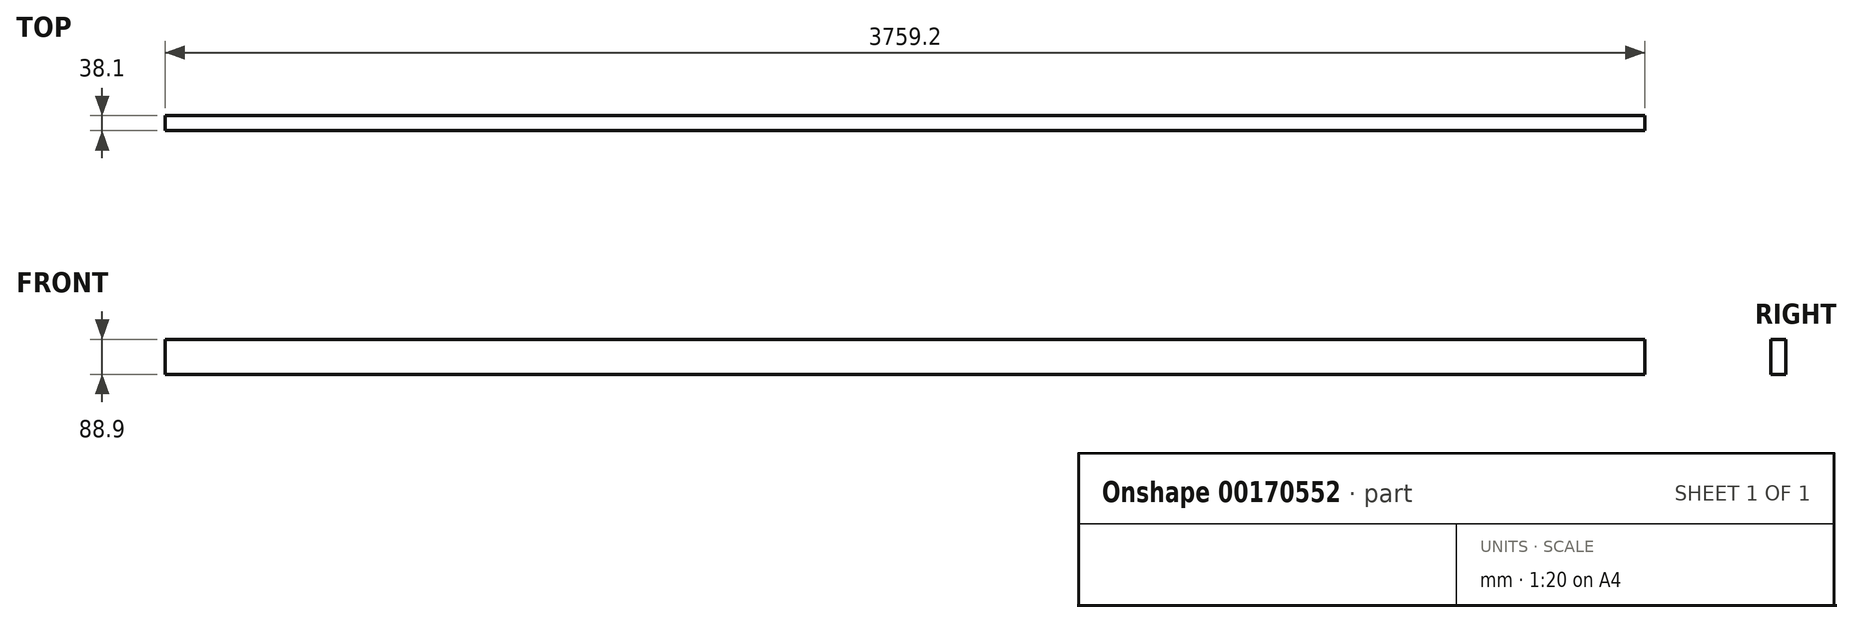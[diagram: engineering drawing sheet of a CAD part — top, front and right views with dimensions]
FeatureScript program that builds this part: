
annotation { "Feature Type Name" : "Feature", "Feature Type Description" : "" }
export const myFeature = defineFeature(function(context is Context, id is Id, definition is map)
    precondition{}
    {
        {
            var Q0;
            Q0=qCreatedBy(makeId("Right.planeOp"),FACE);
            var sketch = newSketch(context, id + "F0", { "sketchPlane" : qUnion([Q0])});
            skLineSegment(sketch, "E0.bottom", {"start": v(0, 0) * mm, "end": v(38.1, 0) * mm});
            skLineSegment(sketch, "E0.top", {"start": v(0, 88.9) * mm, "end": v(38.1, 88.9) * mm});
            skLineSegment(sketch, "E0.left", {"start": v(0, 0) * mm, "end": v(0, 88.9) * mm});
            skLineSegment(sketch, "E0.right", {"start": v(38.1, 0) * mm, "end": v(38.1, 88.9) * mm});
            skSolve(sketch);
        }
        {
            var Q0;
            Q0=makeQuery(id+"F0.imprint","IMPRINT",FACE,{"disambiguationData":[TD([[makeQuery(id+"F0.imprint","IMPRINT",EDGE,{"derivedFrom":sQuery(id+"F0.wireOp",EDGE,"E0.bottom")}),1.0]])]});
            extrude(context, id + "F1", {"entities" : qUnion([Q0]), "depth" : 3759.2 * mm});
        }
    });
